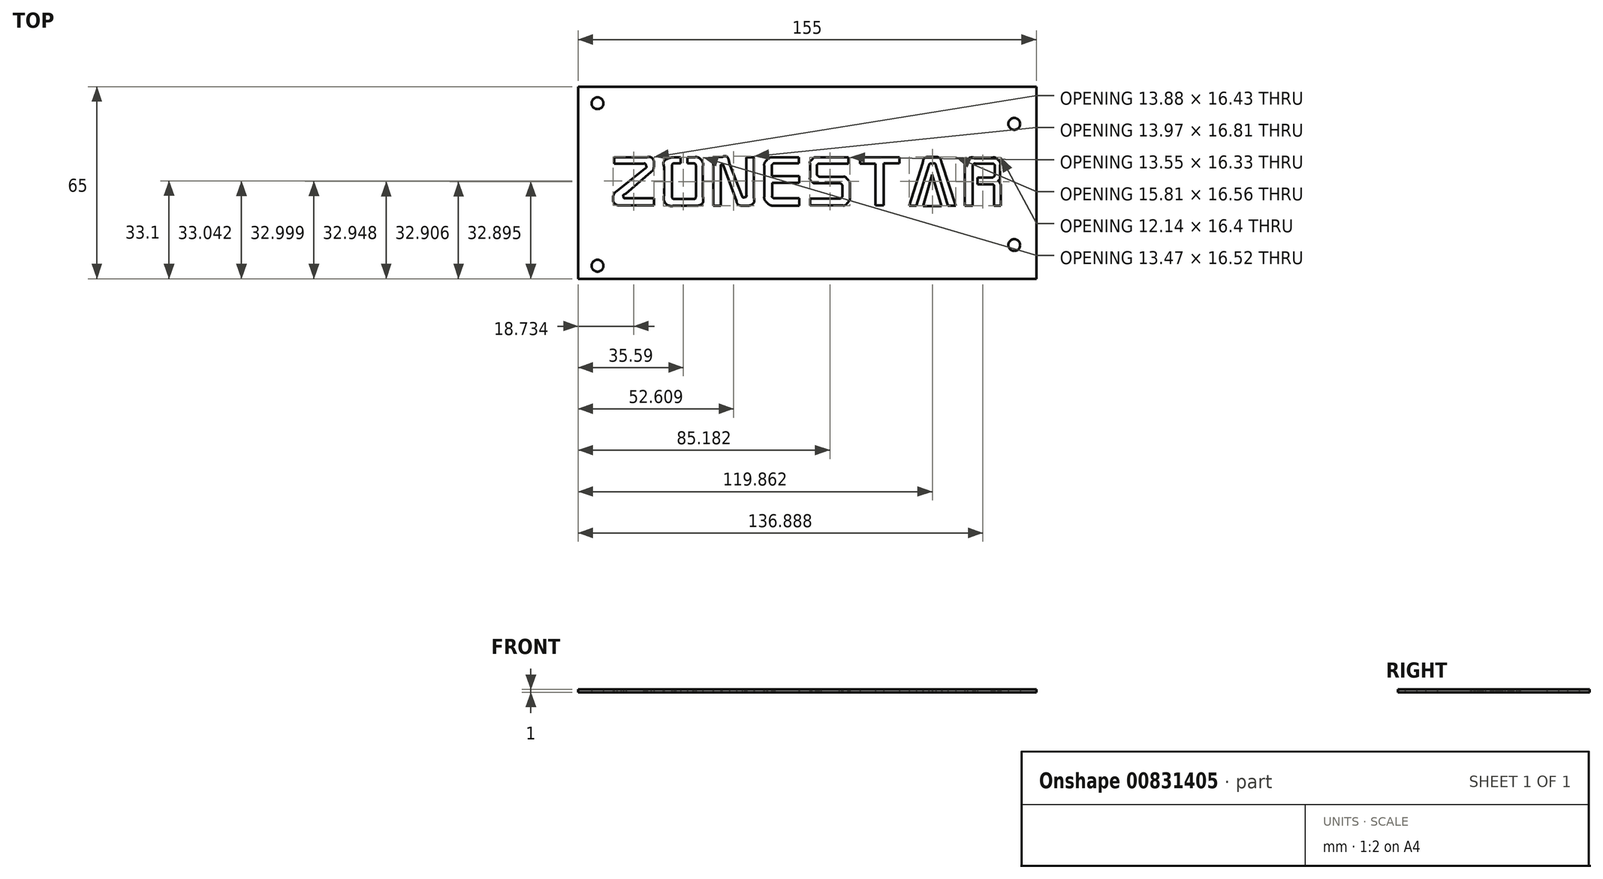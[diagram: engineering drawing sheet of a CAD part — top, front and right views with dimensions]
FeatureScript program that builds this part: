
annotation { "Feature Type Name" : "Feature", "Feature Type Description" : "" }
export const myFeature = defineFeature(function(context is Context, id is Id, definition is map)
    precondition{}
    {
        {
            var Q0;
            Q0=qCreatedBy(makeId("Top.planeOp"),FACE);
            var sketch = newSketch(context, id + "F0", { "sketchPlane" : qUnion([Q0])});
            skLineSegment(sketch, "E0.bottom", {"start": v(-77.4, 32.05) * mm, "end": v(77.6, 32.05) * mm});
            skLineSegment(sketch, "E0.top", {"start": v(-77.4, -32.95) * mm, "end": v(77.6, -32.95) * mm});
            skLineSegment(sketch, "E0.left", {"start": v(-77.4, 32.05) * mm, "end": v(-77.4, -32.95) * mm});
            skLineSegment(sketch, "E0.right", {"start": v(77.6, 32.05) * mm, "end": v(77.6, -32.95) * mm});
            skLineSegment(sketch, "E1", {"start": v(-55.3, 6) * mm, "end": v(-65.17, 6) * mm});
            skLineSegment(sketch, "E2", {"start": v(-65.17, 6) * mm, "end": v(-65.17, 8.17) * mm});
            skLineSegment(sketch, "E3", {"start": v(-65.17, 8.17) * mm, "end": v(-54.03, 8.17) * mm});
            skLineSegment(sketch, "E4", {"start": v(-52.74, 3.25) * mm, "end": v(-61.3, -4.14) * mm});
            skLineSegment(sketch, "E5", {"start": v(-61.17, -5.7) * mm, "end": v(-51.77, -5.7) * mm});
            skLineSegment(sketch, "E6", {"start": v(-51.77, -5.7) * mm, "end": v(-51.77, -8.05) * mm});
            skLineSegment(sketch, "E7", {"start": v(-51.77, -8.05) * mm, "end": v(-62.97, -8.05) * mm});
            skLineSegment(sketch, "E8", {"start": v(-64.35, -3.28) * mm, "end": v(-54.8, 4.32) * mm});
            skLineSegment(sketch, "E9", {"start": v(-40.48, 6.06) * mm, "end": v(-38.64, 6.06) * mm});
            skLineSegment(sketch, "E10", {"start": v(-37.6, 4.93) * mm, "end": v(-37.6, -4.6) * mm});
            skLineSegment(sketch, "E11", {"start": v(-38.73, -5.91) * mm, "end": v(-44.44, -5.91) * mm});
            skLineSegment(sketch, "E12", {"start": v(-45.7, -4.5) * mm, "end": v(-45.7, 5.08) * mm});
            skLineSegment(sketch, "E13", {"start": v(-44.71, 6.06) * mm, "end": v(-42.74, 6.06) * mm});
            skLineSegment(sketch, "E14", {"start": v(-42.74, 6.06) * mm, "end": v(-42.72, 8.1) * mm});
            skLineSegment(sketch, "E15", {"start": v(-42.72, 8.1) * mm, "end": v(-45.03, 8.1) * mm});
            skLineSegment(sketch, "E16", {"start": v(-48.3, 4.7) * mm, "end": v(-48.32, -4.47) * mm});
            skLineSegment(sketch, "E17", {"start": v(-44.7, -8.2) * mm, "end": v(-38.7, -8.2) * mm});
            skLineSegment(sketch, "E18", {"start": v(-35.25, -4.81) * mm, "end": v(-35.25, 4.98) * mm});
            skLineSegment(sketch, "E19", {"start": v(-38.35, 8.1) * mm, "end": v(-40.48, 8.1) * mm});
            skLineSegment(sketch, "E20", {"start": v(-40.48, 8.1) * mm, "end": v(-40.48, 6.06) * mm});
            skLineSegment(sketch, "E21", {"start": v(-29.17, 5.2) * mm, "end": v(-29.17, -8.21) * mm});
            skLineSegment(sketch, "E22", {"start": v(-29.17, -8.21) * mm, "end": v(-31.74, -8.21) * mm});
            skLineSegment(sketch, "E23", {"start": v(-31.74, -8.21) * mm, "end": v(-31.74, 5.91) * mm});
            skLineSegment(sketch, "E24", {"start": v(-26.2, 6.02) * mm, "end": v(-21.94, -5.04) * mm});
            skLineSegment(sketch, "E25", {"start": v(-20.47, -4.71) * mm, "end": v(-20.47, 8.1) * mm});
            skLineSegment(sketch, "E26", {"start": v(-20.47, 8.1) * mm, "end": v(-17.96, 8.1) * mm});
            skLineSegment(sketch, "E27", {"start": v(-17.96, 8.1) * mm, "end": v(-17.96, -5.53) * mm});
            skLineSegment(sketch, "E28", {"start": v(-23.86, -6.74) * mm, "end": v(-28.26, 5.33) * mm});
            skLineSegment(sketch, "E29", {"start": v(-11.05, 6.08) * mm, "end": v(-2.78, 6.08) * mm});
            skLineSegment(sketch, "E30", {"start": v(-2.78, 6.08) * mm, "end": v(-2.78, 8.1) * mm});
            skLineSegment(sketch, "E31", {"start": v(-2.78, 8.1) * mm, "end": v(-11.75, 8.1) * mm});
            skLineSegment(sketch, "E32", {"start": v(-14.47, 5.18) * mm, "end": v(-14.47, -5.04) * mm});
            skLineSegment(sketch, "E33", {"start": v(-11.23, -8.19) * mm, "end": v(-2.63, -8.19) * mm});
            skLineSegment(sketch, "E34", {"start": v(-2.63, -8.19) * mm, "end": v(-2.63, -5.66) * mm});
            skLineSegment(sketch, "E35", {"start": v(-2.63, -5.66) * mm, "end": v(-10.88, -5.66) * mm});
            skLineSegment(sketch, "E36", {"start": v(-11.81, -5) * mm, "end": v(-11.81, -0.46) * mm});
            skLineSegment(sketch, "E37", {"start": v(-11.81, -0.46) * mm, "end": v(-2.63, -0.46) * mm});
            skLineSegment(sketch, "E38", {"start": v(-2.63, -0.46) * mm, "end": v(-2.63, 1.8) * mm});
            skLineSegment(sketch, "E39", {"start": v(-2.63, 1.8) * mm, "end": v(-11.9, 1.8) * mm});
            skLineSegment(sketch, "E40", {"start": v(-11.9, 1.8) * mm, "end": v(-11.9, 4.96) * mm});
            skLineSegment(sketch, "E41", {"start": v(3.18, 8.13) * mm, "end": v(14.04, 8.13) * mm});
            skLineSegment(sketch, "E42", {"start": v(14.04, 8.13) * mm, "end": v(14.04, 6.04) * mm});
            skLineSegment(sketch, "E43", {"start": v(14.04, 6.04) * mm, "end": v(4.13, 6.04) * mm});
            skLineSegment(sketch, "E44", {"start": v(3.37, 5.26) * mm, "end": v(3.37, 2.56) * mm});
            skLineSegment(sketch, "E45", {"start": v(4.73, 1.57) * mm, "end": v(12.1, 1.57) * mm});
            skLineSegment(sketch, "E46", {"start": v(14.51, -1.24) * mm, "end": v(14.51, -5.04) * mm});
            skLineSegment(sketch, "E47", {"start": v(11.96, -8.12) * mm, "end": v(1.04, -8.12) * mm});
            skLineSegment(sketch, "E48", {"start": v(1.04, -8.12) * mm, "end": v(1.04, -5.81) * mm});
            skLineSegment(sketch, "E49", {"start": v(1.04, -5.81) * mm, "end": v(10.86, -5.81) * mm});
            skLineSegment(sketch, "E50", {"start": v(11.94, -4.56) * mm, "end": v(11.94, -1.6) * mm});
            skLineSegment(sketch, "E51", {"start": v(10.82, -0.59) * mm, "end": v(2.83, -0.59) * mm});
            skLineSegment(sketch, "E52", {"start": v(1.02, 1.29) * mm, "end": v(1.02, 6.15) * mm});
            skLineSegment(sketch, "E53", {"start": v(17.95, 8.12) * mm, "end": v(31.3, 8.12) * mm});
            skLineSegment(sketch, "E54", {"start": v(31.3, 8.12) * mm, "end": v(31.3, 6.06) * mm});
            skLineSegment(sketch, "E55", {"start": v(31.3, 6.06) * mm, "end": v(25.92, 6.06) * mm});
            skLineSegment(sketch, "E56", {"start": v(25.92, 6.06) * mm, "end": v(25.92, -8.08) * mm});
            skLineSegment(sketch, "E57", {"start": v(25.92, -8.08) * mm, "end": v(23.22, -8.08) * mm});
            skLineSegment(sketch, "E58", {"start": v(23.22, -8.08) * mm, "end": v(23.22, 6.01) * mm});
            skLineSegment(sketch, "E59", {"start": v(23.22, 6.01) * mm, "end": v(17.93, 6.01) * mm});
            skLineSegment(sketch, "E60", {"start": v(17.93, 6.01) * mm, "end": v(17.95, 8.12) * mm});
            skLineSegment(sketch, "E61", {"start": v(45.6, 6.17) * mm, "end": v(50.36, -8.23) * mm});
            skLineSegment(sketch, "E62", {"start": v(50.36, -8.23) * mm, "end": v(47.63, -8.23) * mm});
            skLineSegment(sketch, "E63", {"start": v(47.63, -8.23) * mm, "end": v(43.64, 5.3) * mm});
            skLineSegment(sketch, "E64", {"start": v(41.26, 5.3) * mm, "end": v(37.05, -8.23) * mm});
            skLineSegment(sketch, "E65", {"start": v(37.05, -8.23) * mm, "end": v(34.55, -8.23) * mm});
            skLineSegment(sketch, "E66", {"start": v(34.55, -8.23) * mm, "end": v(39.2, 6.26) * mm});
            skLineSegment(sketch, "E67", {"start": v(39.27, -8.3) * mm, "end": v(45.47, -8.3) * mm});
            skLineSegment(sketch, "E68", {"start": v(45.47, -8.3) * mm, "end": v(42.4, 2.33) * mm});
            skLineSegment(sketch, "E69", {"start": v(42.4, 2.33) * mm, "end": v(39.27, -8.3) * mm});
            skLineSegment(sketch, "E70", {"start": v(53.44, -8.24) * mm, "end": v(53.44, 5.3) * mm});
            skLineSegment(sketch, "E71", {"start": v(56.49, 8.08) * mm, "end": v(62.86, 8.11) * mm});
            skLineSegment(sketch, "E72", {"start": v(65.39, 5.54) * mm, "end": v(65.39, 1.07) * mm});
            skLineSegment(sketch, "E73", {"start": v(65.54, -1.58) * mm, "end": v(65.54, -8.25) * mm});
            skLineSegment(sketch, "E74", {"start": v(65.54, -8.25) * mm, "end": v(63.35, -8.25) * mm});
            skLineSegment(sketch, "E75", {"start": v(63.35, -8.25) * mm, "end": v(63.35, -1.67) * mm});
            skLineSegment(sketch, "E76", {"start": v(62.58, -0.98) * mm, "end": v(57.72, -0.98) * mm});
            skLineSegment(sketch, "E77", {"start": v(57.72, -0.98) * mm, "end": v(57.71, 1.33) * mm});
            skLineSegment(sketch, "E78", {"start": v(57.71, 1.33) * mm, "end": v(62.45, 1.33) * mm});
            skLineSegment(sketch, "E79", {"start": v(63.6, 2.5) * mm, "end": v(63.6, 5.07) * mm});
            skLineSegment(sketch, "E80", {"start": v(62.34, 6.04) * mm, "end": v(56.96, 6.04) * mm});
            skLineSegment(sketch, "E81", {"start": v(56.06, 4.85) * mm, "end": v(56.06, -8.23) * mm});
            skLineSegment(sketch, "E82", {"start": v(56.06, -8.23) * mm, "end": v(53.44, -8.24) * mm});
            skFitSpline(sketch, "E83", {"points": [v(-54.03, 8.17) * mm, v(-52.8, 8.23) * mm, v(-51.8, 6.85) * mm, v(-51.8, 5.79) * mm]});
            skFitSpline(sketch, "E84", {"points": [v(-51.8, 5.79) * mm, v(-51.8, 4.9) * mm, v(-52.07, 3.9) * mm, v(-52.74, 3.25) * mm]});
            skFitSpline(sketch, "E85", {"points": [v(-61.3, -4.14) * mm, v(-61.3, -4.14) * mm, v(-61.3, -4.14) * mm, v(-61.34, -4.17) * mm, v(-62.19, -4.7) * mm, v(-62.03, -5.2) * mm]});
            skFitSpline(sketch, "E86", {"points": [v(-62.03, -5.2) * mm, v(-61.88, -5.68) * mm, v(-61.24, -5.7) * mm, v(-61.17, -5.7) * mm, v(-61.17, -5.7) * mm, v(-61.17, -5.7) * mm]});
            skFitSpline(sketch, "E87", {"points": [v(-62.97, -8.05) * mm, v(-64.04, -8.08) * mm, v(-65.5, -7) * mm, v(-65.54, -5.94) * mm]});
            skFitSpline(sketch, "E88", {"points": [v(-65.54, -5.94) * mm, v(-65.57, -5.07) * mm, v(-64.99, -3.83) * mm, v(-64.35, -3.28) * mm]});
            skFitSpline(sketch, "E89", {"points": [v(-54.8, 4.32) * mm, v(-54.42, 4.62) * mm, v(-54.34, 4.94) * mm, v(-54.42, 5.27) * mm]});
            skFitSpline(sketch, "E90", {"points": [v(-54.42, 5.27) * mm, v(-54.52, 5.64) * mm, v(-54.8, 6.06) * mm, v(-55.3, 6) * mm]});
            skFitSpline(sketch, "E91", {"points": [v(-38.64, 6.06) * mm, v(-37.95, 6.05) * mm, v(-37.6, 5.49) * mm, v(-37.6, 4.93) * mm]});
            skFitSpline(sketch, "E92", {"points": [v(-37.6, -4.6) * mm, v(-37.64, -5.47) * mm, v(-37.94, -5.91) * mm, v(-38.73, -5.91) * mm]});
            skFitSpline(sketch, "E93", {"points": [v(-44.44, -5.91) * mm, v(-45.27, -5.9) * mm, v(-45.63, -5.37) * mm, v(-45.7, -4.5) * mm]});
            skFitSpline(sketch, "E94", {"points": [v(-45.7, 5.08) * mm, v(-45.7, 5.46) * mm, v(-45.32, 6.06) * mm, v(-44.71, 6.06) * mm]});
            skFitSpline(sketch, "E95", {"points": [v(-45.03, 8.1) * mm, v(-45.98, 8.1) * mm, v(-48.35, 6.87) * mm, v(-48.3, 4.7) * mm]});
            skFitSpline(sketch, "E96", {"points": [v(-48.32, -4.47) * mm, v(-48.25, -6.88) * mm, v(-46.81, -8.2) * mm, v(-44.7, -8.2) * mm]});
            skFitSpline(sketch, "E97", {"points": [v(-38.7, -8.2) * mm, v(-36.7, -8.16) * mm, v(-35.27, -7.36) * mm, v(-35.25, -4.81) * mm]});
            skFitSpline(sketch, "E98", {"points": [v(-35.25, 4.98) * mm, v(-35.25, 6.43) * mm, v(-36.83, 8.1) * mm, v(-38.35, 8.1) * mm]});
            skFitSpline(sketch, "E99", {"points": [v(-31.74, 5.91) * mm, v(-31.68, 7.36) * mm, v(-30.71, 8.21) * mm, v(-28.83, 8.26) * mm]});
            skFitSpline(sketch, "E100", {"points": [v(-28.83, 8.26) * mm, v(-27, 8.32) * mm, v(-26.23, 6.14) * mm, v(-26.2, 6.02) * mm, v(-26.2, 6.02) * mm, v(-26.2, 6.02) * mm]});
            skFitSpline(sketch, "E101", {"points": [v(-21.94, -5.04) * mm, v(-21.83, -5.26) * mm, v(-21.55, -5.45) * mm, v(-21.09, -5.37) * mm]});
            skFitSpline(sketch, "E102", {"points": [v(-21.09, -5.37) * mm, v(-20.67, -5.29) * mm, v(-20.47, -5.05) * mm, v(-20.47, -4.71) * mm]});
            skFitSpline(sketch, "E103", {"points": [v(-17.96, -5.53) * mm, v(-17.94, -7.17) * mm, v(-19.6, -8.2) * mm, v(-20.91, -8.2) * mm]});
            skFitSpline(sketch, "E104", {"points": [v(-20.91, -8.2) * mm, v(-22.21, -8.2) * mm, v(-23.4, -7.8) * mm, v(-23.86, -6.74) * mm]});
            skFitSpline(sketch, "E105", {"points": [v(-28.26, 5.33) * mm, v(-28.4, 5.64) * mm, v(-28.56, 5.8) * mm, v(-28.78, 5.76) * mm]});
            skFitSpline(sketch, "E106", {"points": [v(-28.78, 5.76) * mm, v(-29, 5.73) * mm, v(-29.17, 5.48) * mm, v(-29.17, 5.2) * mm]});
            skFitSpline(sketch, "E107", {"points": [v(-11.75, 8.1) * mm, v(-12.52, 8.07) * mm, v(-13.13, 7.69) * mm, v(-13.62, 7.18) * mm]});
            skFitSpline(sketch, "E108", {"points": [v(-13.62, 7.18) * mm, v(-14.1, 6.68) * mm, v(-14.47, 5.88) * mm, v(-14.47, 5.18) * mm]});
            skFitSpline(sketch, "E109", {"points": [v(-14.47, -5.04) * mm, v(-14.45, -5.86) * mm, v(-14.03, -6.68) * mm, v(-13.45, -7.24) * mm]});
            skFitSpline(sketch, "E110", {"points": [v(-13.45, -7.24) * mm, v(-12.87, -7.8) * mm, v(-12, -8.16) * mm, v(-11.23, -8.19) * mm]});
            skFitSpline(sketch, "E111", {"points": [v(-10.88, -5.66) * mm, v(-11.17, -5.66) * mm, v(-11.38, -5.64) * mm, v(-11.54, -5.5) * mm]});
            skFitSpline(sketch, "E112", {"points": [v(-11.54, -5.5) * mm, v(-11.7, -5.38) * mm, v(-11.82, -5.24) * mm, v(-11.81, -5) * mm]});
            skFitSpline(sketch, "E113", {"points": [v(-11.9, 4.96) * mm, v(-11.9, 5.27) * mm, v(-11.86, 5.54) * mm, v(-11.7, 5.74) * mm]});
            skFitSpline(sketch, "E114", {"points": [v(-11.7, 5.74) * mm, v(-11.54, 5.94) * mm, v(-11.35, 6.08) * mm, v(-11.05, 6.08) * mm]});
            skFitSpline(sketch, "E115", {"points": [v(4.13, 6.04) * mm, v(3.85, 6.02) * mm, v(3.72, 5.94) * mm, v(3.59, 5.8) * mm]});
            skFitSpline(sketch, "E116", {"points": [v(3.59, 5.8) * mm, v(3.45, 5.66) * mm, v(3.36, 5.48) * mm, v(3.37, 5.26) * mm]});
            skFitSpline(sketch, "E117", {"points": [v(3.37, 2.56) * mm, v(3.4, 2.17) * mm, v(3.53, 2.02) * mm, v(3.76, 1.85) * mm]});
            skFitSpline(sketch, "E118", {"points": [v(3.76, 1.85) * mm, v(4, 1.67) * mm, v(4.27, 1.57) * mm, v(4.73, 1.57) * mm]});
            skFitSpline(sketch, "E119", {"points": [v(12.1, 1.57) * mm, v(12.84, 1.57) * mm, v(13.36, 1.12) * mm, v(13.79, 0.63) * mm]});
            skFitSpline(sketch, "E120", {"points": [v(13.79, 0.63) * mm, v(14.22, 0.14) * mm, v(14.51, -0.44) * mm, v(14.51, -1.24) * mm]});
            skFitSpline(sketch, "E121", {"points": [v(14.51, -5.04) * mm, v(14.51, -6.12) * mm, v(14.28, -6.56) * mm, v(13.84, -7.1) * mm]});
            skFitSpline(sketch, "E122", {"points": [v(13.84, -7.1) * mm, v(13.4, -7.65) * mm, v(12.78, -8.12) * mm, v(11.96, -8.12) * mm]});
            skFitSpline(sketch, "E123", {"points": [v(10.86, -5.81) * mm, v(11.33, -5.81) * mm, v(11.52, -5.61) * mm, v(11.73, -5.4) * mm]});
            skFitSpline(sketch, "E124", {"points": [v(11.73, -5.4) * mm, v(11.93, -5.18) * mm, v(11.94, -5.02) * mm, v(11.94, -4.56) * mm]});
            skFitSpline(sketch, "E125", {"points": [v(11.94, -1.6) * mm, v(11.94, -1.25) * mm, v(11.86, -1.1) * mm, v(11.67, -0.92) * mm]});
            skFitSpline(sketch, "E126", {"points": [v(11.67, -0.92) * mm, v(11.48, -0.73) * mm, v(11.25, -0.59) * mm, v(10.82, -0.59) * mm]});
            skFitSpline(sketch, "E127", {"points": [v(2.83, -0.59) * mm, v(2.21, -0.57) * mm, v(1.82, -0.28) * mm, v(1.5, 0.06) * mm]});
            skFitSpline(sketch, "E128", {"points": [v(1.5, 0.06) * mm, v(1.2, 0.39) * mm, v(1.02, 0.77) * mm, v(1.02, 1.29) * mm]});
            skFitSpline(sketch, "E129", {"points": [v(1.02, 6.15) * mm, v(1.04, 6.77) * mm, v(1.24, 6.95) * mm, v(1.6, 7.31) * mm]});
            skFitSpline(sketch, "E130", {"points": [v(1.6, 7.31) * mm, v(1.96, 7.68) * mm, v(2.4, 8.1) * mm, v(3.18, 8.13) * mm]});
            skFitSpline(sketch, "E131", {"points": [v(39.2, 6.26) * mm, v(39.7, 7.84) * mm, v(41.11, 8.32) * mm, v(42.39, 8.3) * mm]});
            skFitSpline(sketch, "E132", {"points": [v(42.39, 8.3) * mm, v(43.66, 8.3) * mm, v(44.95, 7.88) * mm, v(45.6, 6.17) * mm]});
            skFitSpline(sketch, "E133", {"points": [v(43.64, 5.3) * mm, v(43.4, 6) * mm, v(42.9, 6.07) * mm, v(42.47, 6.06) * mm]});
            skFitSpline(sketch, "E134", {"points": [v(42.47, 6.06) * mm, v(42.04, 6.06) * mm, v(41.52, 5.98) * mm, v(41.26, 5.3) * mm]});
            skFitSpline(sketch, "E135", {"points": [v(53.44, 5.3) * mm, v(53.44, 6.37) * mm, v(53.68, 6.78) * mm, v(54.23, 7.3) * mm]});
            skFitSpline(sketch, "E136", {"points": [v(54.23, 7.3) * mm, v(54.77, 7.83) * mm, v(55.33, 8.08) * mm, v(56.49, 8.08) * mm]});
            skFitSpline(sketch, "E137", {"points": [v(62.86, 8.11) * mm, v(63.6, 8.11) * mm, v(64.2, 7.77) * mm, v(64.64, 7.32) * mm]});
            skFitSpline(sketch, "E138", {"points": [v(64.64, 7.32) * mm, v(65.08, 6.87) * mm, v(65.39, 6.32) * mm, v(65.39, 5.54) * mm]});
            skFitSpline(sketch, "E139", {"points": [v(65.39, 1.07) * mm, v(65.39, 0.84) * mm, v(65.24, 0.66) * mm, v(65.11, 0.54) * mm]});
            skFitSpline(sketch, "E140", {"points": [v(65.11, 0.54) * mm, v(65, 0.42) * mm, v(64.67, 0.25) * mm, v(64.63, 0.23) * mm, v(64.63, 0.23) * mm, v(64.63, 0.23) * mm]});
            skFitSpline(sketch, "E141", {"points": [v(64.63, 0.23) * mm, v(64.63, 0.23) * mm, v(64.63, 0.23) * mm, v(64.68, 0.2) * mm, v(65.13, -0.19) * mm, v(65.28, -0.47) * mm]});
            skFitSpline(sketch, "E142", {"points": [v(65.28, -0.47) * mm, v(65.44, -0.77) * mm, v(65.54, -1.1) * mm, v(65.54, -1.58) * mm]});
            skFitSpline(sketch, "E143", {"points": [v(63.35, -1.67) * mm, v(63.35, -1.42) * mm, v(63.26, -1.3) * mm, v(63.13, -1.16) * mm]});
            skFitSpline(sketch, "E144", {"points": [v(63.13, -1.16) * mm, v(63, -1.03) * mm, v(62.84, -0.98) * mm, v(62.58, -0.98) * mm]});
            skFitSpline(sketch, "E145", {"points": [v(62.45, 1.33) * mm, v(62.84, 1.33) * mm, v(63.04, 1.44) * mm, v(63.26, 1.64) * mm]});
            skFitSpline(sketch, "E146", {"points": [v(63.26, 1.64) * mm, v(63.47, 1.84) * mm, v(63.6, 2.14) * mm, v(63.6, 2.5) * mm]});
            skFitSpline(sketch, "E147", {"points": [v(63.6, 5.07) * mm, v(63.6, 5.44) * mm, v(63.47, 5.67) * mm, v(63.25, 5.85) * mm]});
            skFitSpline(sketch, "E148", {"points": [v(63.25, 5.85) * mm, v(63.03, 6.03) * mm, v(62.82, 6.04) * mm, v(62.34, 6.04) * mm]});
            skFitSpline(sketch, "E149", {"points": [v(56.96, 6.04) * mm, v(56.59, 6.04) * mm, v(56.37, 5.88) * mm, v(56.22, 5.65) * mm]});
            skFitSpline(sketch, "E150", {"points": [v(56.22, 5.65) * mm, v(56.08, 5.43) * mm, v(56.06, 5.21) * mm, v(56.06, 4.85) * mm]});
            skCircle(sketch, "E151", {"center": v(-70.86, 26.46) * mm, "radius": 2 * mm});
            skCircle(sketch, "E152", {"center": v(-70.86, -28.54) * mm, "radius": 2 * mm});
            skCircle(sketch, "E153", {"center": v(70.14, 19.46) * mm, "radius": 2 * mm});
            skCircle(sketch, "E154", {"center": v(70.14, -21.54) * mm, "radius": 2 * mm});
            skSolve(sketch);
        }
        {
            var Q0;
            Q0 = qSketchRegion(id + "F0", true);
            extrude(context, id + "F1", {"entities" : qUnion([Q0]), "depth" : 1 * mm, "offsetDistance" : 25 * mm});
        }
    });
